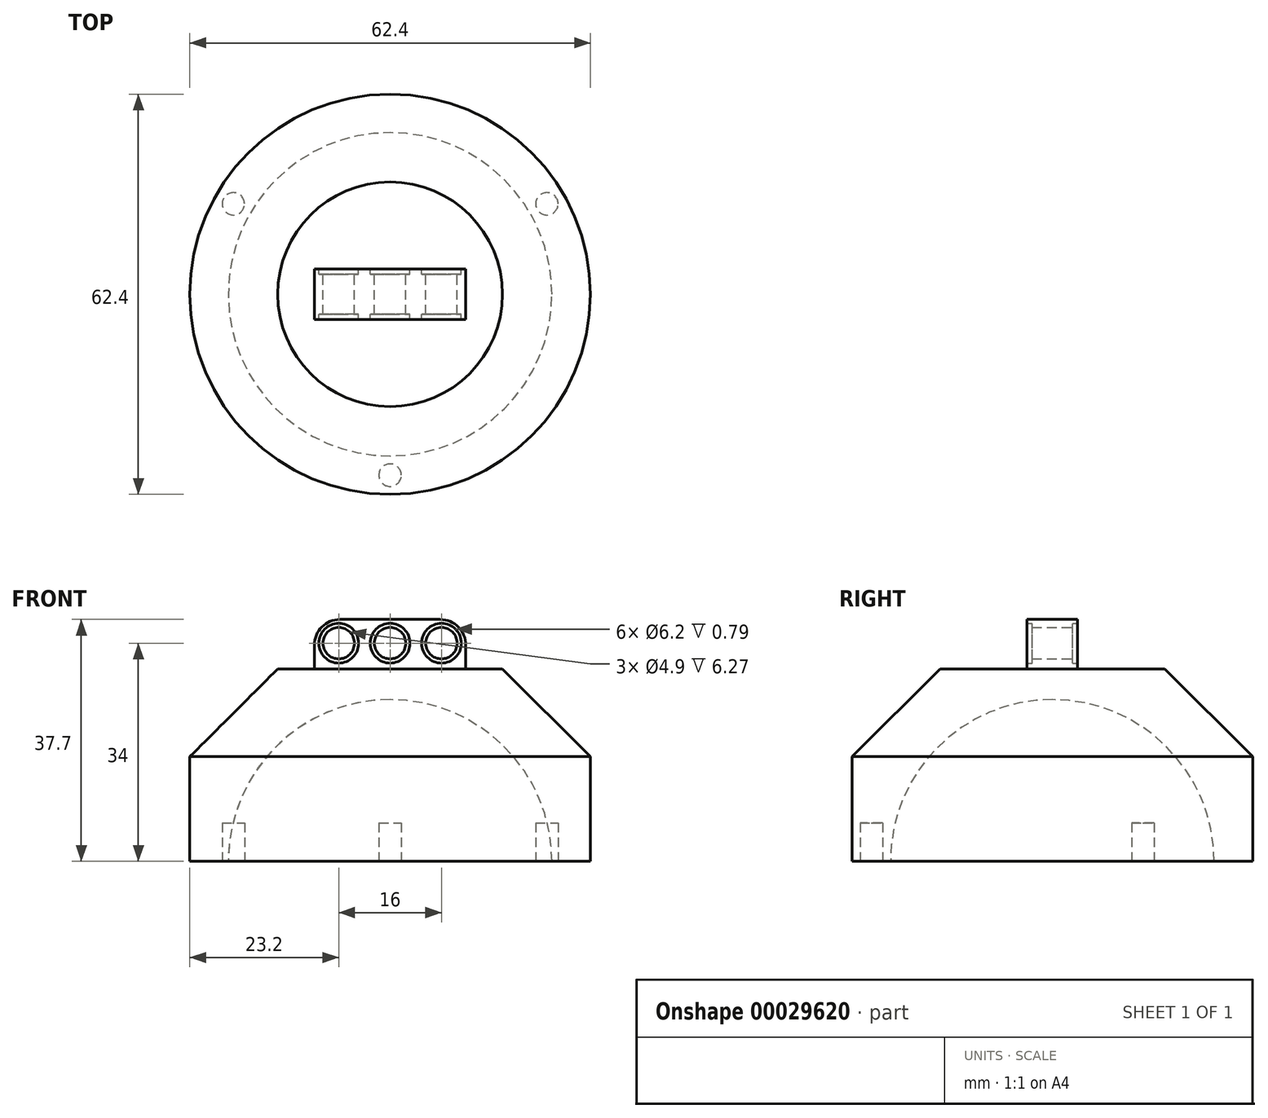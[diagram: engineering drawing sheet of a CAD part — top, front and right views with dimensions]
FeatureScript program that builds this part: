
annotation { "Feature Type Name" : "Feature", "Feature Type Description" : "" }
export const myFeature = defineFeature(function(context is Context, id is Id, definition is map)
    precondition{}
    {
        {
            var Q0;
            Q0=qCreatedBy(makeId("Front.planeOp"),FACE);
            var sketch = newSketch(context, id + "F0", { "sketchPlane" : qUnion([Q0])});
            skArc(sketch, "E0", {"start": v(0, 25.2) * mm, "mid": v(-17.82, 17.82) * mm, "end": v(-25.2, 0) * mm});
            skLineSegment(sketch, "E1.rect.bottom", {"start": v(0, 30) * mm, "end": v(-17.5, 30) * mm});
            skLineSegment(sketch, "E1.rect.right", {"start": v(-31.2, 16.3) * mm, "end": v(-31.2, 0) * mm});
            skLineSegment(sketch, "E2", {"start": v(-25.2, 0) * mm, "end": v(-31.2, 0) * mm});
            skLineSegment(sketch, "E3", {"start": v(0, 0) * mm, "end": v(0, 30) * mm, "construction": true});
            skLineSegment(sketch, "E4", {"start": v(0, 30) * mm, "end": v(0, 25.2) * mm});
            skLineSegment(sketch, "E5", {"start": v(-17.5, 30) * mm, "end": v(-31.2, 16.3) * mm});
            skSolve(sketch);
        }
        {
            var Q0;
            Q0=makeQuery(id+"F0.imprint","IMPRINT",FACE,{"disambiguationData":[TD([[makeQuery(id+"F0.imprint","IMPRINT",EDGE,{"derivedFrom":sQuery(id+"F0.wireOp",EDGE,"E0")}),-1.0]])]});
            var Q1;
            Q1=sQuery(id+"F0.wireOp",EDGE,"E3");
            revolve(context, id + "F1", {"entities" : qUnion([Q0]), "axis" : qUnion([Q1]), "revolveType" : RevolveType.FULL});
        }
        {
            var Q0;
            Q0=qCreatedBy(makeId("Front.planeOp"),FACE);
            var sketch = newSketch(context, id + "F2", { "sketchPlane" : qUnion([Q0])});
            skLineSegment(sketch, "E6.bottom", {"start": v(-11.8, 30) * mm, "end": v(11.8, 30) * mm});
            skLineSegment(sketch, "E6.top", {"start": v(-7.8, 37.7) * mm, "end": v(7.8, 37.7) * mm});
            skLineSegment(sketch, "E6.left", {"start": v(-11.8, 30) * mm, "end": v(-11.8, 33.7) * mm});
            skLineSegment(sketch, "E6.right", {"start": v(11.8, 30) * mm, "end": v(11.8, 33.7) * mm});
            skLineSegment(sketch, "E7", {"start": v(0, 0) * mm, "end": v(0, 75.4) * mm, "construction": true});
            skPoint(sketch, "E8", {"position": v(0, 37.7) * mm});
            skPoint(sketch, "E9.visualSharp", {"position": v(-11.8, 37.7) * mm});
            skArc(sketch, "E9.filletArc", {"start": v(-7.8, 37.7) * mm, "mid": v(-10.63, 36.53) * mm, "end": v(-11.8, 33.7) * mm});
            skPoint(sketch, "E10.visualSharp", {"position": v(11.8, 37.7) * mm});
            skArc(sketch, "E10.filletArc", {"start": v(11.8, 33.7) * mm, "mid": v(10.63, 36.53) * mm, "end": v(7.8, 37.7) * mm});
            skLineSegment(sketch, "E11", {"start": v(35.17, 34) * mm, "end": v(-28.97, 34) * mm, "construction": true});
            skCircle(sketch, "E12", {"center": v(0, 34) * mm, "radius": 3.1 * mm});
            skCircle(sketch, "E13", {"center": v(-8, 34) * mm, "radius": 3.1 * mm});
            skCircle(sketch, "E14", {"center": v(8, 34) * mm, "radius": 3.1 * mm});
            skSolve(sketch);
        }
        {
            var Q0;
            Q0 = qSketchRegion(id + "F2", true);
            extrude(context, id + "F3", {"entities" : qUnion([Q0]), "operationType" : NewBodyOperationType.ADD, "endBound" : BoundingType.SYMMETRIC, "depth" : 7.85 * mm});
        }
        {
            var Q0;
            Q0=makeQuery(id+"F1.opRevolve","SWEPT_FACE",FACE,{"disambiguationData":[OSD([sQuery(id+"F0.wireOp",EDGE,"E2")])]});
            var sketch = newSketch(context, id + "F4", { "sketchPlane" : qUnion([Q0])});
            skCircle(sketch, "E15", {"center": v(0, 28.2) * mm, "radius": 1.75 * mm});
            skCircle(sketch, "E16.1.0", {"center": v(-24.42, -14.1) * mm, "radius": 1.75 * mm});
            skCircle(sketch, "E16.2.0", {"center": v(24.42, -14.1) * mm, "radius": 1.75 * mm});
            skPoint(sketch, "E16.center", {"position": v(0, 0) * mm});
            skSolve(sketch);
        }
        {
            var Q0;
            Q0 = qSketchRegion(id + "F4", true);
            extrude(context, id + "F5", {"entities" : qUnion([Q0]), "operationType" : NewBodyOperationType.REMOVE, "oppositeDirection" : true, "depth" : 6 * mm});
        }
        {
            var Q0;
            Q0=qCreatedBy(makeId("Front.planeOp"),FACE);
            var sketch = newSketch(context, id + "F6", { "sketchPlane" : qUnion([Q0])});
            skLineSegment(sketch, "E17", {"start": v(0, 29.78) * mm, "end": v(0, 40.81) * mm, "construction": true});
            skCircle(sketch, "E18", {"center": v(0, 34) * mm, "radius": 2.45 * mm});
            skCircle(sketch, "E19", {"center": v(0, 34) * mm, "radius": 3.37 * mm});
            skCircle(sketch, "E20", {"center": v(8, 34) * mm, "radius": 2.45 * mm});
            skCircle(sketch, "E21", {"center": v(8, 34) * mm, "radius": 3.34 * mm});
            skCircle(sketch, "E22", {"center": v(-8, 34) * mm, "radius": 3.34 * mm});
            skCircle(sketch, "E23", {"center": v(-8, 34) * mm, "radius": 2.45 * mm});
            skSolve(sketch);
        }
        {
            var Q0;
            Q0 = qSketchRegion(id + "F6", true);
            extrude(context, id + "F7", {"entities" : qUnion([Q0]), "operationType" : NewBodyOperationType.ADD, "endBound" : BoundingType.SYMMETRIC, "depth" : 6.27 * mm});
        }
    });
